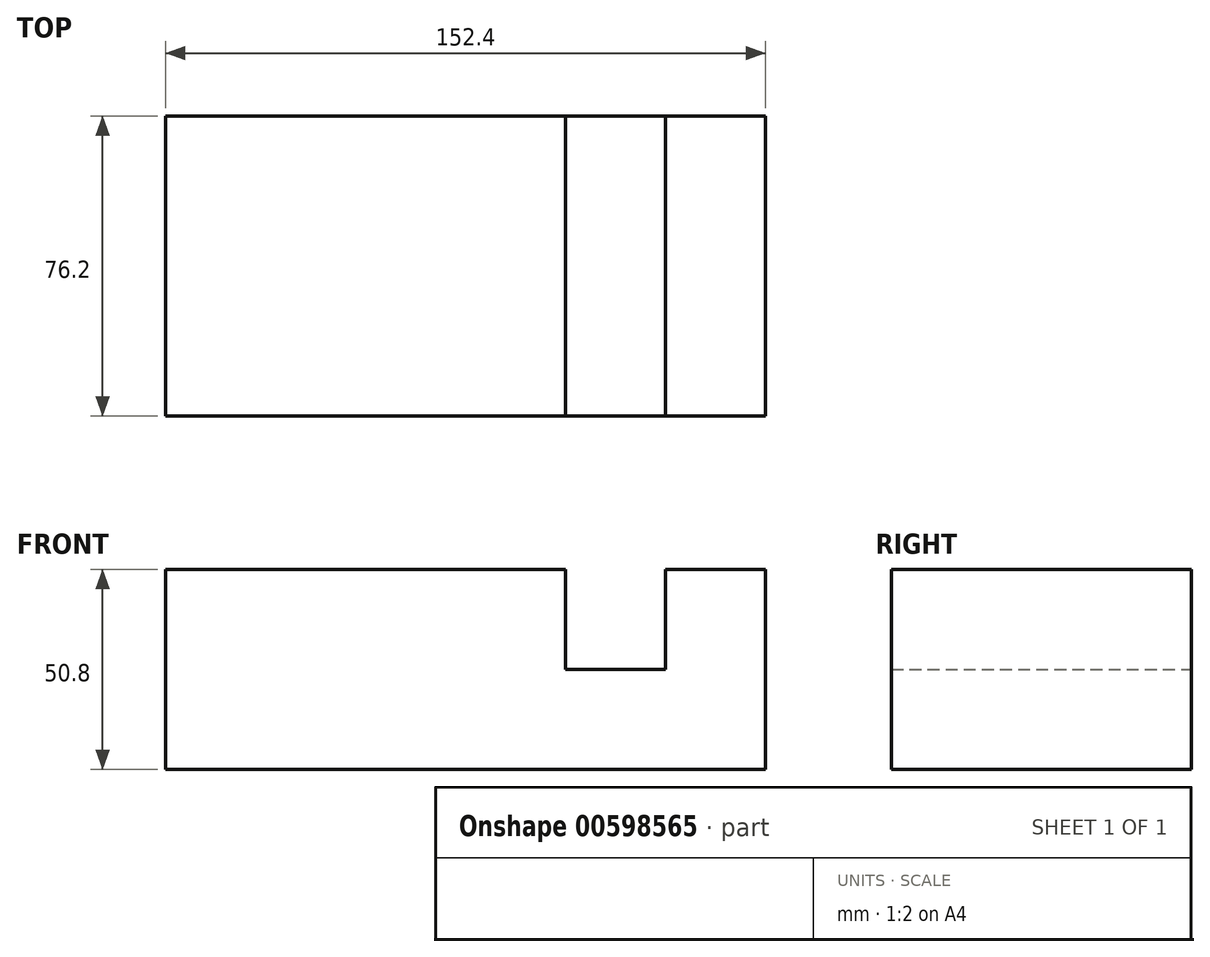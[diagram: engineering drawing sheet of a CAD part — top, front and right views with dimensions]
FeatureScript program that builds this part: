
annotation { "Feature Type Name" : "Feature", "Feature Type Description" : "" }
export const myFeature = defineFeature(function(context is Context, id is Id, definition is map)
    precondition{}
    {
        {
            var Q0;
            Q0=qCreatedBy(makeId("Front.planeOp"),FACE);
            var sketch = newSketch(context, id + "F0", { "sketchPlane" : qUnion([Q0])});
            skLineSegment(sketch, "E0", {"start": v(0, 0) * mm, "end": v(152.4, 0) * mm});
            skLineSegment(sketch, "E1", {"start": v(152.4, 0) * mm, "end": v(152.4, 50.8) * mm});
            skLineSegment(sketch, "E2", {"start": v(152.4, 50.8) * mm, "end": v(127, 50.8) * mm});
            skLineSegment(sketch, "E3", {"start": v(127, 50.8) * mm, "end": v(127, 25.4) * mm});
            skLineSegment(sketch, "E4", {"start": v(127, 25.4) * mm, "end": v(101.6, 25.4) * mm});
            skLineSegment(sketch, "E5", {"start": v(101.6, 25.4) * mm, "end": v(101.6, 50.8) * mm});
            skLineSegment(sketch, "E6", {"start": v(101.6, 50.8) * mm, "end": v(0, 50.8) * mm});
            skLineSegment(sketch, "E7", {"start": v(0, 50.8) * mm, "end": v(0, 0) * mm});
            skSolve(sketch);
        }
        {
            var Q0;
            Q0 = qSketchRegion(id + "F0", true);
            extrude(context, id + "F1", {"entities" : qUnion([Q0]), "depth" : 76.2 * mm, "offsetDistance" : 25.4 * mm});
        }
    });
